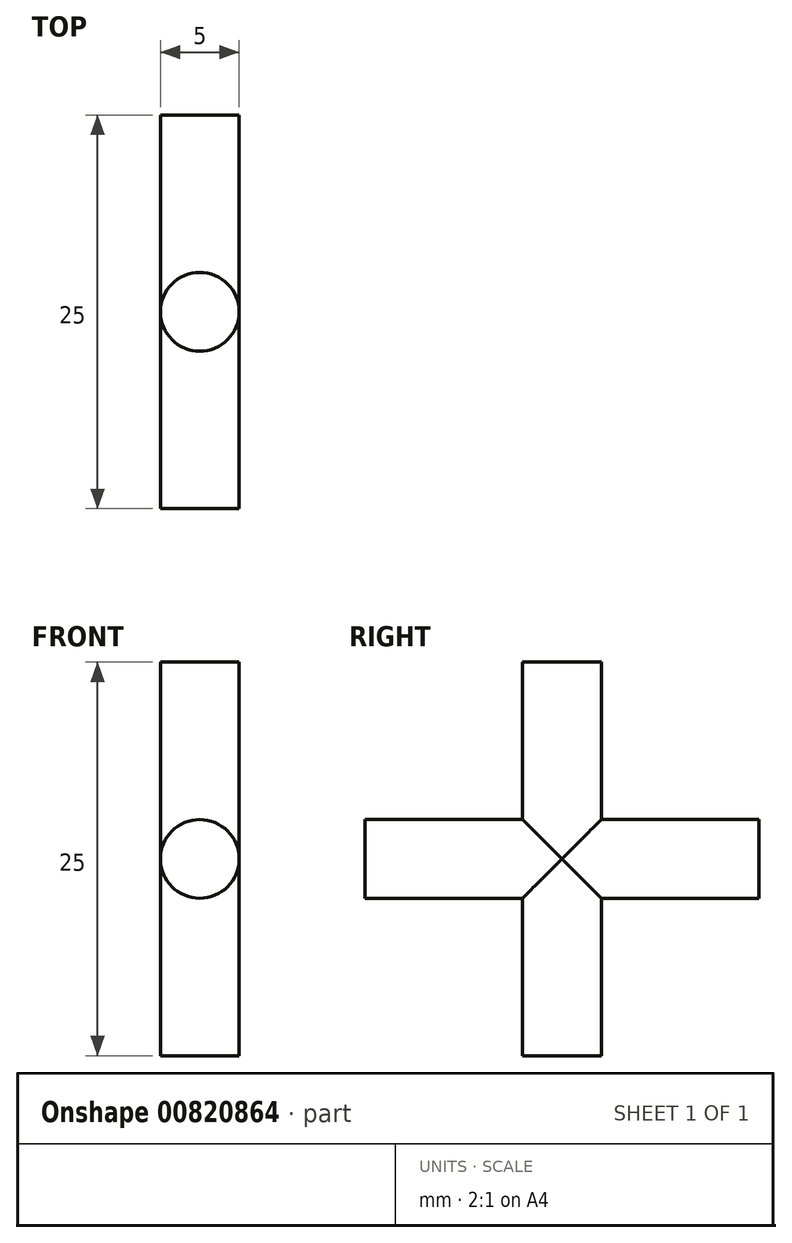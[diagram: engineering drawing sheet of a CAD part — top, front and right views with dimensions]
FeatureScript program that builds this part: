
annotation { "Feature Type Name" : "Feature", "Feature Type Description" : "" }
export const myFeature = defineFeature(function(context is Context, id is Id, definition is map)
    precondition{}
    {
        {
            var Q0;
            Q0=qCreatedBy(makeId("Top.planeOp"),FACE);
            var sketch = newSketch(context, id + "F0", { "sketchPlane" : qUnion([Q0])});
            skCircle(sketch, "E0", {"center": v(0, 0) * mm, "radius": 2.5 * mm});
            skSolve(sketch);
        }
        {
            var Q0;
            Q0 = qSketchRegion(id + "F0", true);
            extrude(context, id + "F1", {"entities" : qUnion([Q0]), "endBound" : BoundingType.SYMMETRIC, "oppositeDirection" : true, "depth" : 25 * mm, "offsetDistance" : 25 * mm});
        }
        {
            var Q0;
            Q0=qCreatedBy(makeId("Front.planeOp"),FACE);
            var sketch = newSketch(context, id + "F2", { "sketchPlane" : qUnion([Q0])});
            skCircle(sketch, "E1", {"center": v(0, 0) * mm, "radius": 2.5 * mm});
            skSolve(sketch);
        }
        {
            var Q0;
            Q0 = qSketchRegion(id + "F2", true);
            extrude(context, id + "F3", {"entities" : qUnion([Q0]), "operationType" : NewBodyOperationType.ADD, "endBound" : BoundingType.SYMMETRIC, "depth" : 25 * mm, "offsetDistance" : 25 * mm});
        }
    });
